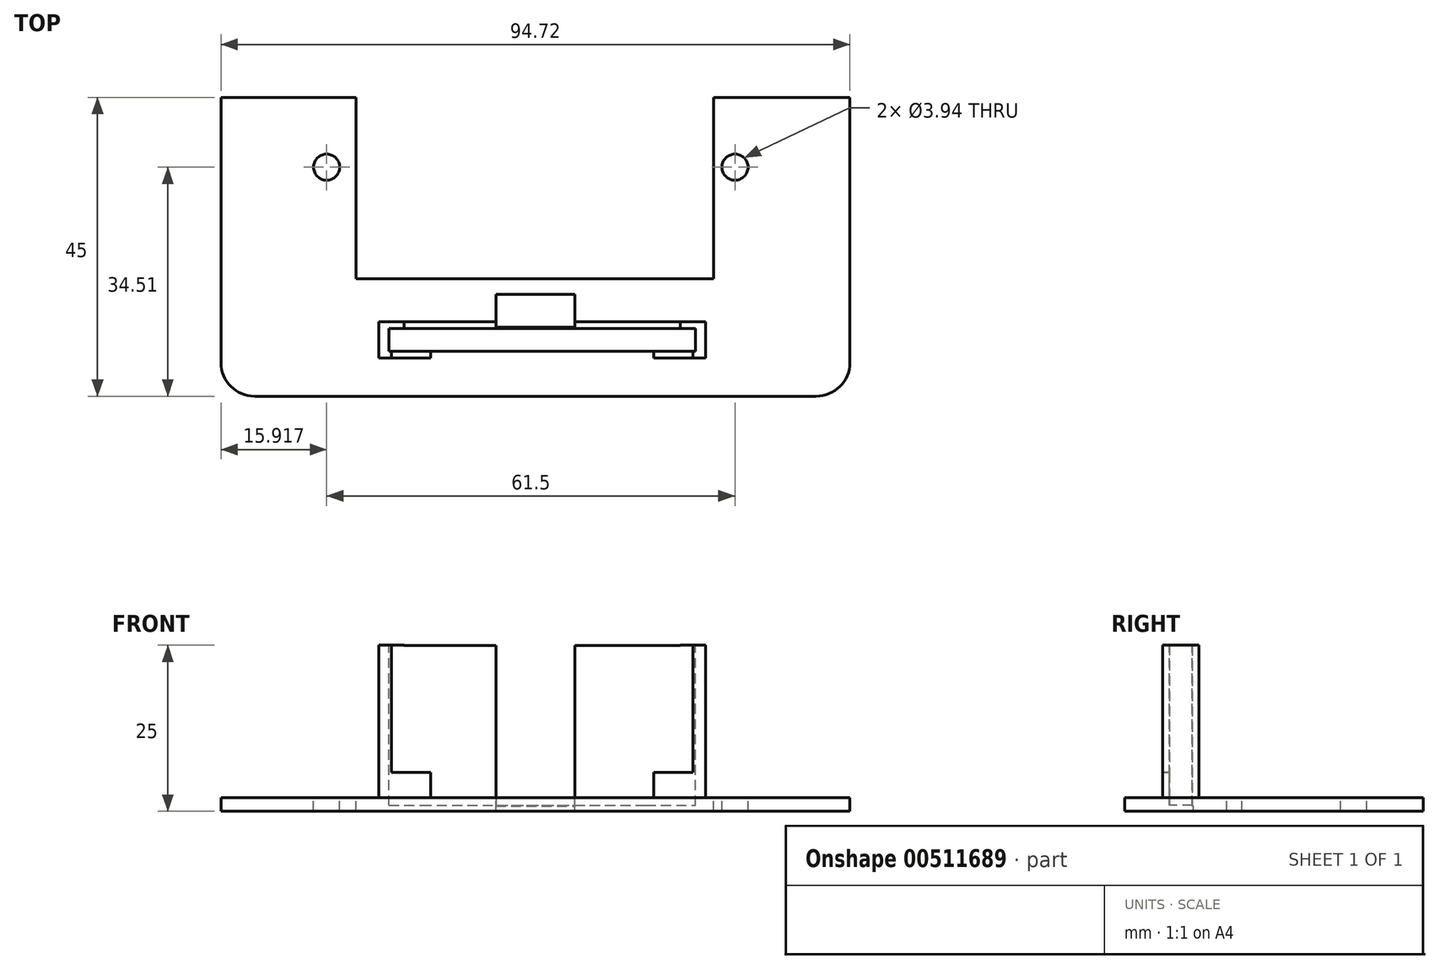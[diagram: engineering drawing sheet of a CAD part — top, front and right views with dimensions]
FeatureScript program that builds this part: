
annotation { "Feature Type Name" : "Feature", "Feature Type Description" : "" }
export const myFeature = defineFeature(function(context is Context, id is Id, definition is map)
    precondition{}
    {
        {
            var Q0;
            Q0=qCreatedBy(makeId("Top.planeOp"),FACE);
            var sketch = newSketch(context, id + "F0", { "sketchPlane" : qUnion([Q0])});
            skLineSegment(sketch, "E0.bottom", {"start": v(-47.36, 22.5) * mm, "end": v(47.36, 22.5) * mm});
            skLineSegment(sketch, "E0.top", {"start": v(-47.36, -22.5) * mm, "end": v(47.36, -22.5) * mm});
            skLineSegment(sketch, "E0.left", {"start": v(-47.36, 22.5) * mm, "end": v(-47.36, -22.5) * mm});
            skLineSegment(sketch, "E0.right", {"start": v(47.36, 22.5) * mm, "end": v(47.36, -22.5) * mm});
            skPoint(sketch, "E0.middle", {"position": v(0, 0) * mm});
            skSolve(sketch);
        }
        {
            var Q0;
            Q0 = qSketchRegion(id + "F0", true);
            extrude(context, id + "F1", {"entities" : qUnion([Q0]), "depth" : 2 * mm, "offsetDistance" : 25.4 * mm});
        }
        {
            var Q0;
            Q0=makeQuery(id+"F1.opExtrude","CAP_FACE",FACE,{"disambiguationData":[OSD([sQuery(id+"F0.wireOp",EDGE,"E0.bottom"),sQuery(id+"F0.wireOp",EDGE,"E0.top"),sQuery(id+"F0.wireOp",EDGE,"E0.left"),sQuery(id+"F0.wireOp",EDGE,"E0.right")])],"isStart":false});
            var sketch = newSketch(context, id + "F2", { "sketchPlane" : qUnion([Q0])});
            skPoint(sketch, "E1", {"position": v(-31.44, 12.01) * mm});
            skPoint(sketch, "E2", {"position": v(30.06, 12.01) * mm});
            skSolve(sketch);
        }
        {
            var Q0;
            Q0=sQuery(id+"F2.wireOp",VERTEX,"E1");
            var Q1;
            Q1=sQuery(id+"F2.wireOp",VERTEX,"E2");
            var Q2;
            Q2=makeQuery(id+"F1.opExtrude","SWEPT_BODY",BODY,{"disambiguationData":[OSD([sQuery(id+"F0.wireOp",EDGE,"E0.bottom"),sQuery(id+"F0.wireOp",EDGE,"E0.top"),sQuery(id+"F0.wireOp",EDGE,"E0.left"),sQuery(id+"F0.wireOp",EDGE,"E0.right")])]});
            hole(context, id + "F3", {"style" : HoleStyle.SIMPLE, "endStyle" : HoleEndStyle.BLIND, "holeDiameter" : 3.94 * mm, "holeDepth" : 25.4 * mm, "isTappedThrough" : true, "tappedDepth" : 12.7 * mm, "tapClearance" : 3, "locations" : qUnion([Q0, Q1]), "scope" : qUnion([Q2])});
        }
        {
            var Q0;
            Q0=makeQuery(id+"F1.opExtrude","CAP_FACE",FACE,{"disambiguationData":[OSD([sQuery(id+"F0.wireOp",EDGE,"E0.bottom"),sQuery(id+"F0.wireOp",EDGE,"E0.top"),sQuery(id+"F0.wireOp",EDGE,"E0.left"),sQuery(id+"F0.wireOp",EDGE,"E0.right")])],"isStart":false});
            var sketch = newSketch(context, id + "F4", { "sketchPlane" : qUnion([Q0])});
            skPoint(sketch, "E3", {"position": v(-31.44, 12.01) * mm});
            skPoint(sketch, "E4", {"position": v(30.06, 12.01) * mm});
            skPoint(sketch, "E5", {"position": v(-27, 12.01) * mm});
            skPoint(sketch, "E6", {"position": v(26.8, 12.01) * mm});
            skLineSegment(sketch, "E7.bottom", {"start": v(-27, 22.5) * mm, "end": v(26.8, 22.5) * mm});
            skLineSegment(sketch, "E7.top", {"start": v(-27, -4.83) * mm, "end": v(26.8, -4.83) * mm});
            skLineSegment(sketch, "E7.left", {"start": v(-27, 22.5) * mm, "end": v(-27, -4.83) * mm});
            skLineSegment(sketch, "E7.right", {"start": v(26.8, 22.5) * mm, "end": v(26.8, -4.83) * mm});
            skSolve(sketch);
        }
        {
            var Q0;
            Q0 = qSketchRegion(id + "F4", true);
            extrude(context, id + "F5", {"entities" : qUnion([Q0]), "operationType" : NewBodyOperationType.REMOVE, "oppositeDirection" : true, "depth" : 25.4 * mm, "offsetDistance" : 25.4 * mm});
        }
        {
            var Q0;
            Q0=makeQuery(id+"F1.opExtrude","CAP_FACE",FACE,{"disambiguationData":[OSD([sQuery(id+"F0.wireOp",EDGE,"E0.bottom"),sQuery(id+"F0.wireOp",EDGE,"E0.top"),sQuery(id+"F0.wireOp",EDGE,"E0.left"),sQuery(id+"F0.wireOp",EDGE,"E0.right")])],"isStart":false});
            var sketch = newSketch(context, id + "F6", { "sketchPlane" : qUnion([Q0])});
            skLineSegment(sketch, "E8.bottom", {"start": v(-5.95, -7.12) * mm, "end": v(5.95, -7.12) * mm});
            skLineSegment(sketch, "E8.top", {"start": v(-5.95, -12.12) * mm, "end": v(5.95, -12.12) * mm});
            skLineSegment(sketch, "E8.left", {"start": v(-5.95, -7.12) * mm, "end": v(-5.95, -12.12) * mm});
            skLineSegment(sketch, "E8.right", {"start": v(5.95, -7.12) * mm, "end": v(5.95, -12.12) * mm});
            skPoint(sketch, "E8.middle", {"position": v(0, -9.62) * mm});
            skSolve(sketch);
        }
        {
            var Q0;
            Q0 = qSketchRegion(id + "F6", true);
            extrude(context, id + "F7", {"entities" : qUnion([Q0]), "operationType" : NewBodyOperationType.REMOVE, "oppositeDirection" : true, "depth" : 25.4 * mm, "offsetDistance" : 25.4 * mm});
        }
        {
            var Q0;
            Q0=makeQuery(id+"F1.opExtrude","CAP_FACE",FACE,{"disambiguationData":[OSD([sQuery(id+"F0.wireOp",EDGE,"E0.bottom"),sQuery(id+"F0.wireOp",EDGE,"E0.top"),sQuery(id+"F0.wireOp",EDGE,"E0.left"),sQuery(id+"F0.wireOp",EDGE,"E0.right")])],"isStart":false});
            var sketch = newSketch(context, id + "F8", { "sketchPlane" : qUnion([Q0])});
            skPoint(sketch, "E9", {"position": v(0, -9.62) * mm});
            skPoint(sketch, "E9.positionSnap0", {"position": v(-5.95, -9.62) * mm});
            skPoint(sketch, "E9.positionSnap1", {"position": v(0, -12.12) * mm});
            skLineSegment(sketch, "E10", {"start": v(-25.2, -12.12) * mm, "end": v(24.93, -12.12) * mm});
            skPoint(sketch, "E11", {"position": v(0, -14.01) * mm});
            skPoint(sketch, "E12", {"position": v(-21.7, -14.01) * mm});
            skPoint(sketch, "E13", {"position": v(23.75, -14.01) * mm});
            skLineSegment(sketch, "E14.bottom", {"start": v(-23.6, -11.26) * mm, "end": v(-19.8, -11.26) * mm});
            skLineSegment(sketch, "E14.top", {"start": v(-23.6, -16.76) * mm, "end": v(-19.8, -16.76) * mm});
            skLineSegment(sketch, "E14.left", {"start": v(-23.6, -11.26) * mm, "end": v(-23.6, -16.76) * mm});
            skLineSegment(sketch, "E14.right", {"start": v(-19.8, -11.26) * mm, "end": v(-19.8, -16.76) * mm});
            skLineSegment(sketch, "E15.bottom", {"start": v(21.84, -16.76) * mm, "end": v(25.65, -16.76) * mm});
            skLineSegment(sketch, "E15.top", {"start": v(21.84, -11.26) * mm, "end": v(25.65, -11.26) * mm});
            skLineSegment(sketch, "E15.left", {"start": v(21.84, -16.76) * mm, "end": v(21.84, -11.26) * mm});
            skLineSegment(sketch, "E15.right", {"start": v(25.65, -16.76) * mm, "end": v(25.65, -11.26) * mm});
            skSolve(sketch);
        }
        {
            var Q0;
            Q0 = qSketchRegion(id + "F8", true);
            extrude(context, id + "F9", {"entities" : qUnion([Q0]), "operationType" : NewBodyOperationType.ADD, "depth" : 23 * mm, "offsetDistance" : 25.4 * mm});
        }
        {
            var Q0;
            Q0=makeQuery(id+"F9.opExtrude","CAP_FACE",FACE,{"disambiguationData":[OSD([sQuery(id+"F8.wireOp",EDGE,"E14.bottom"),sQuery(id+"F8.wireOp",EDGE,"E14.top"),sQuery(id+"F8.wireOp",EDGE,"E14.left"),sQuery(id+"F8.wireOp",EDGE,"E14.right")])],"isStart":false});
            var sketch = newSketch(context, id + "F10", { "sketchPlane" : qUnion([Q0])});
            skLineSegment(sketch, "E16.bottom", {"start": v(-22.05, -12.3) * mm, "end": v(-17.53, -12.3) * mm});
            skLineSegment(sketch, "E16.top", {"start": v(-22.05, -15.72) * mm, "end": v(-17.53, -15.72) * mm});
            skLineSegment(sketch, "E16.left", {"start": v(-22.05, -12.3) * mm, "end": v(-22.05, -15.72) * mm});
            skLineSegment(sketch, "E16.right", {"start": v(-17.53, -12.3) * mm, "end": v(-17.53, -15.72) * mm});
            skPoint(sketch, "E16.middle", {"position": v(-19.8, -14.01) * mm});
            skSolve(sketch);
        }
        {
            var Q0;
            Q0 = qSketchRegion(id + "F10", true);
            extrude(context, id + "F11", {"entities" : qUnion([Q0]), "operationType" : NewBodyOperationType.REMOVE, "oppositeDirection" : true, "depth" : 22.86 * mm, "offsetDistance" : 25.4 * mm});
        }
        {
            var Q0;
            Q0=makeQuery(id+"F9.opExtrude","CAP_FACE",FACE,{"disambiguationData":[OSD([sQuery(id+"F8.wireOp",EDGE,"E15.bottom"),sQuery(id+"F8.wireOp",EDGE,"E15.top"),sQuery(id+"F8.wireOp",EDGE,"E15.left"),sQuery(id+"F8.wireOp",EDGE,"E15.right")])],"isStart":false});
            var sketch = newSketch(context, id + "F12", { "sketchPlane" : qUnion([Q0])});
            skLineSegment(sketch, "E17.bottom", {"start": v(24.1, -12.3) * mm, "end": v(19.58, -12.3) * mm});
            skLineSegment(sketch, "E17.top", {"start": v(24.1, -15.73) * mm, "end": v(19.58, -15.73) * mm});
            skLineSegment(sketch, "E17.left", {"start": v(24.1, -12.3) * mm, "end": v(24.1, -15.73) * mm});
            skLineSegment(sketch, "E17.right", {"start": v(19.58, -12.3) * mm, "end": v(19.58, -15.73) * mm});
            skPoint(sketch, "E17.middle", {"position": v(21.84, -14.01) * mm});
            skSolve(sketch);
        }
        {
            var Q0;
            Q0 = qSketchRegion(id + "F12", true);
            extrude(context, id + "F13", {"entities" : qUnion([Q0]), "operationType" : NewBodyOperationType.REMOVE, "oppositeDirection" : true, "depth" : 22.86 * mm, "offsetDistance" : 25.4 * mm});
        }
        {
            var Q0;
            Q0=makeQuery(id+"F11.boolean.opBoolean","COPY",FACE,{"derivedFrom":makeQuery(id+"F11.opExtrude","CAP_FACE",FACE,{"disambiguationData":[OSD([sQuery(id+"F10.wireOp",EDGE,"E16.bottom"),sQuery(id+"F10.wireOp",EDGE,"E16.top"),sQuery(id+"F10.wireOp",EDGE,"E16.left"),sQuery(id+"F10.wireOp",EDGE,"E16.right")])],"isStart":false})});
            var sketch = newSketch(context, id + "F14", { "sketchPlane" : qUnion([Q0])});
            skLineSegment(sketch, "E18.bottom", {"start": v(-22.05, -12.3) * mm, "end": v(16.62, -12.3) * mm});
            skLineSegment(sketch, "E18.top", {"start": v(-22.05, -15.72) * mm, "end": v(16.62, -15.72) * mm});
            skLineSegment(sketch, "E18.left", {"start": v(-22.05, -12.3) * mm, "end": v(-22.05, -15.72) * mm});
            skLineSegment(sketch, "E18.right", {"start": v(16.62, -12.3) * mm, "end": v(16.62, -15.72) * mm});
            skSolve(sketch);
        }
        {
            var Q0;
            Q0 = qSketchRegion(id + "F14", true);
            extrude(context, id + "F15", {"entities" : qUnion([Q0]), "operationType" : NewBodyOperationType.REMOVE, "oppositeDirection" : true, "depth" : 1.27 * mm, "offsetDistance" : 25.4 * mm});
        }
        {
            var Q0;
            Q0=makeQuery(id+"F13.boolean.opBoolean","COPY",FACE,{"derivedFrom":makeQuery(id+"F13.opExtrude","CAP_FACE",FACE,{"disambiguationData":[OSD([sQuery(id+"F12.wireOp",EDGE,"E17.bottom"),sQuery(id+"F12.wireOp",EDGE,"E17.top"),sQuery(id+"F12.wireOp",EDGE,"E17.left"),sQuery(id+"F12.wireOp",EDGE,"E17.right")])],"isStart":false})});
            var sketch = newSketch(context, id + "F16", { "sketchPlane" : qUnion([Q0])});
            skPoint(sketch, "E19.oppositeSnap0", {"position": v(22.97, -15.73) * mm});
            skLineSegment(sketch, "E19.bottom", {"start": v(24.1, -12.3) * mm, "end": v(-17.13, -12.3) * mm});
            skLineSegment(sketch, "E19.top", {"start": v(24.1, -15.73) * mm, "end": v(-17.13, -15.73) * mm});
            skLineSegment(sketch, "E19.left", {"start": v(24.1, -12.3) * mm, "end": v(24.1, -15.73) * mm});
            skLineSegment(sketch, "E19.right", {"start": v(-17.13, -12.3) * mm, "end": v(-17.13, -15.73) * mm});
            skSolve(sketch);
        }
        {
            var Q0;
            Q0 = qSketchRegion(id + "F16", true);
            extrude(context, id + "F17", {"entities" : qUnion([Q0]), "operationType" : NewBodyOperationType.REMOVE, "oppositeDirection" : true, "depth" : 1.27 * mm, "offsetDistance" : 25.4 * mm});
        }
        {
            var Q0;
            Q0=makeQuery(id+"F1.opExtrude","CAP_FACE",FACE,{"disambiguationData":[OSD([sQuery(id+"F0.wireOp",EDGE,"E0.bottom"),sQuery(id+"F0.wireOp",EDGE,"E0.top"),sQuery(id+"F0.wireOp",EDGE,"E0.left"),sQuery(id+"F0.wireOp",EDGE,"E0.right")])],"isStart":false});
            var sketch = newSketch(context, id + "F18", { "sketchPlane" : qUnion([Q0])});
            skLineSegment(sketch, "E20.bottom", {"start": v(-19.8, -11.26) * mm, "end": v(-5.95, -11.26) * mm});
            skLineSegment(sketch, "E20.top", {"start": v(-19.8, -12.3) * mm, "end": v(-5.95, -12.3) * mm});
            skLineSegment(sketch, "E20.left", {"start": v(-19.8, -11.26) * mm, "end": v(-19.8, -12.3) * mm});
            skLineSegment(sketch, "E20.right", {"start": v(-5.95, -11.26) * mm, "end": v(-5.95, -12.3) * mm});
            skSolve(sketch);
        }
        {
            var Q0;
            Q0 = qSketchRegion(id + "F18", true);
            extrude(context, id + "F19", {"entities" : qUnion([Q0]), "operationType" : NewBodyOperationType.ADD, "depth" : 22.96 * mm, "offsetDistance" : 25.4 * mm});
        }
        {
            var Q0;
            Q0=makeQuery(id+"F1.opExtrude","CAP_FACE",FACE,{"disambiguationData":[OSD([sQuery(id+"F0.wireOp",EDGE,"E0.bottom"),sQuery(id+"F0.wireOp",EDGE,"E0.top"),sQuery(id+"F0.wireOp",EDGE,"E0.left"),sQuery(id+"F0.wireOp",EDGE,"E0.right")])],"isStart":false});
            var sketch = newSketch(context, id + "F20", { "sketchPlane" : qUnion([Q0])});
            skLineSegment(sketch, "E21.bottom", {"start": v(21.84, -12.3) * mm, "end": v(5.95, -12.3) * mm});
            skLineSegment(sketch, "E21.top", {"start": v(21.84, -11.26) * mm, "end": v(5.95, -11.26) * mm});
            skLineSegment(sketch, "E21.left", {"start": v(21.84, -12.3) * mm, "end": v(21.84, -11.26) * mm});
            skLineSegment(sketch, "E21.right", {"start": v(5.95, -12.3) * mm, "end": v(5.95, -11.26) * mm});
            skSolve(sketch);
        }
        {
            var Q0;
            Q0 = qSketchRegion(id + "F20", true);
            extrude(context, id + "F21", {"entities" : qUnion([Q0]), "operationType" : NewBodyOperationType.ADD, "depth" : 22.96 * mm, "offsetDistance" : 25.4 * mm});
        }
        {
            var Q0;
            {var subQ5=makeQuery(id+"F1.opExtrude","CAP_FACE",FACE,{"disambiguationData":[OSD([sQuery(id+"F0.wireOp",EDGE,"E0.bottom"),sQuery(id+"F0.wireOp",EDGE,"E0.top"),sQuery(id+"F0.wireOp",EDGE,"E0.left"),sQuery(id+"F0.wireOp",EDGE,"E0.right")])],"isStart":false});var subQ8=subQ5;Q0=makeQuery(id+"F21.boolean.opBoolean","SPLIT",FACE,{"disambiguationData":[TD([makeQuery(id+"F7.boolean.opBoolean","COPY",FACE,{"derivedFrom":makeQuery(id+"F7.opExtrude","SWEPT_FACE",FACE,{"disambiguationData":[OSD([sQuery(id+"F6.wireOp",EDGE,"E8.top")])]})})])],"derivedFrom":subQ8});}
            var sketch = newSketch(context, id + "F22", { "sketchPlane" : qUnion([Q0])});
            skLineSegment(sketch, "E22.bottom", {"start": v(-5.95, -12.3) * mm, "end": v(5.95, -12.3) * mm});
            skLineSegment(sketch, "E22.top", {"start": v(-5.95, -12.12) * mm, "end": v(5.95, -12.12) * mm});
            skLineSegment(sketch, "E22.left", {"start": v(-5.95, -12.3) * mm, "end": v(-5.95, -12.12) * mm});
            skLineSegment(sketch, "E22.right", {"start": v(5.95, -12.3) * mm, "end": v(5.95, -12.12) * mm});
            skSolve(sketch);
        }
        {
            var Q0;
            Q0 = qSketchRegion(id + "F22", true);
            extrude(context, id + "F23", {"entities" : qUnion([Q0]), "operationType" : NewBodyOperationType.REMOVE, "oppositeDirection" : true, "depth" : 1.27 * mm, "offsetDistance" : 25.4 * mm});
        }
        {
            var Q0;
            {var subQ0=sQuery(id+"F0.wireOp",EDGE,"E0.top");var subQ1=sQuery(id+"F0.wireOp",EDGE,"E0.left");var subQ2=sQuery(id+"F0.wireOp",EDGE,"E0.right");var subQ3=sQuery(id+"F0.wireOp",EDGE,"E0.bottom");Q0=makeQuery(id+"F21.boolean.opBoolean","SPLIT",FACE,{"disambiguationData":[TD([makeQuery(id+"F1.opExtrude","SWEPT_FACE",FACE,{"disambiguationData":[OSD([subQ3])]})])],"derivedFrom":makeQuery(id+"F1.opExtrude","CAP_FACE",FACE,{"disambiguationData":[OSD([subQ3,subQ0,subQ1,subQ2])],"isStart":false})});}
            var sketch = newSketch(context, id + "F24", { "sketchPlane" : qUnion([Q0])});
            skLineSegment(sketch, "E23.bottom", {"start": v(-19.8, -16.76) * mm, "end": v(-15.8, -16.76) * mm});
            skLineSegment(sketch, "E23.top", {"start": v(-19.8, -15.72) * mm, "end": v(-15.8, -15.72) * mm});
            skLineSegment(sketch, "E23.left", {"start": v(-19.8, -16.76) * mm, "end": v(-19.8, -15.72) * mm});
            skLineSegment(sketch, "E23.right", {"start": v(-15.8, -16.76) * mm, "end": v(-15.8, -15.72) * mm});
            skLineSegment(sketch, "E24.bottom", {"start": v(21.84, -16.76) * mm, "end": v(17.84, -16.76) * mm});
            skLineSegment(sketch, "E24.top", {"start": v(21.84, -15.72) * mm, "end": v(17.84, -15.72) * mm});
            skLineSegment(sketch, "E24.left", {"start": v(21.84, -16.76) * mm, "end": v(21.84, -15.72) * mm});
            skLineSegment(sketch, "E24.right", {"start": v(17.84, -16.76) * mm, "end": v(17.84, -15.72) * mm});
            skSolve(sketch);
        }
        {
            var Q0;
            Q0 = qSketchRegion(id + "F24", true);
            extrude(context, id + "F25", {"entities" : qUnion([Q0]), "operationType" : NewBodyOperationType.ADD, "depth" : 3.8 * mm, "offsetDistance" : 25.4 * mm});
        }
        {
            var Q0;
            Q0=makeQuery(id+"F25.boolean.opBoolean","MERGE",FACE,{"derivedFrom":[makeQuery(id+"F9.opExtrude","SWEPT_FACE",FACE,{"disambiguationData":[OSD([sQuery(id+"F8.wireOp",EDGE,"E14.top")])]}),makeQuery(id+"F25.opExtrude","SWEPT_FACE",FACE,{"disambiguationData":[OSD([sQuery(id+"F24.wireOp",EDGE,"E23.bottom")])]})]});
            var sketch = newSketch(context, id + "F26", { "sketchPlane" : qUnion([Q0])});
            skPoint(sketch, "E25.oppositeSnap0", {"position": v(-21.7, 25) * mm});
            skLineSegment(sketch, "E25.bottom", {"start": v(-19.8, 25) * mm, "end": v(-21.7, 25) * mm});
            skLineSegment(sketch, "E25.top", {"start": v(-19.8, 5.81) * mm, "end": v(-21.7, 5.81) * mm});
            skLineSegment(sketch, "E25.left", {"start": v(-19.8, 25) * mm, "end": v(-19.8, 5.81) * mm});
            skLineSegment(sketch, "E25.right", {"start": v(-21.7, 25) * mm, "end": v(-21.7, 5.81) * mm});
            skSolve(sketch);
        }
        {
            var Q0;
            Q0 = qSketchRegion(id + "F26", true);
            extrude(context, id + "F27", {"entities" : qUnion([Q0]), "operationType" : NewBodyOperationType.REMOVE, "oppositeDirection" : true, "depth" : 1.45 * mm, "offsetDistance" : 25.4 * mm});
        }
        {
            var Q0;
            Q0=makeQuery(id+"F25.boolean.opBoolean","MERGE",FACE,{"derivedFrom":[makeQuery(id+"F9.opExtrude","SWEPT_FACE",FACE,{"disambiguationData":[OSD([sQuery(id+"F8.wireOp",EDGE,"E15.bottom")])]}),makeQuery(id+"F25.opExtrude","SWEPT_FACE",FACE,{"disambiguationData":[OSD([sQuery(id+"F24.wireOp",EDGE,"E24.bottom")])]})]});
            var sketch = newSketch(context, id + "F28", { "sketchPlane" : qUnion([Q0])});
            skLineSegment(sketch, "E26.bottom", {"start": v(21.84, 5.8) * mm, "end": v(23.75, 5.8) * mm});
            skLineSegment(sketch, "E26.top", {"start": v(21.84, 25) * mm, "end": v(23.75, 25) * mm});
            skLineSegment(sketch, "E26.left", {"start": v(21.84, 5.8) * mm, "end": v(21.84, 25) * mm});
            skLineSegment(sketch, "E26.right", {"start": v(23.75, 5.8) * mm, "end": v(23.75, 25) * mm});
            skSolve(sketch);
        }
        {
            var Q0;
            Q0 = qSketchRegion(id + "F28", true);
            extrude(context, id + "F29", {"entities" : qUnion([Q0]), "operationType" : NewBodyOperationType.REMOVE, "oppositeDirection" : true, "depth" : 1.55 * mm, "offsetDistance" : 25.4 * mm});
        }
        {
            var Q0;
            Q0=makeQuery(id+"F1.opExtrude","SWEPT_EDGE",EDGE,{"disambiguationData":[OSD([sQuery(id+"F0.wireOp",EDGE,"E0.top"),sQuery(id+"F0.wireOp",EDGE,"E0.left")])]});
            var Q1;
            Q1=makeQuery(id+"F1.opExtrude","SWEPT_EDGE",EDGE,{"disambiguationData":[OSD([sQuery(id+"F0.wireOp",EDGE,"E0.top"),sQuery(id+"F0.wireOp",EDGE,"E0.right")])]});
            fillet(context, id + "F30", {"entities" : qUnion([Q0, Q1]), "radius" : 5.08 * mm, "tangentPropagation" : true, "allowEdgeOverflow" : false});
        }
    });
